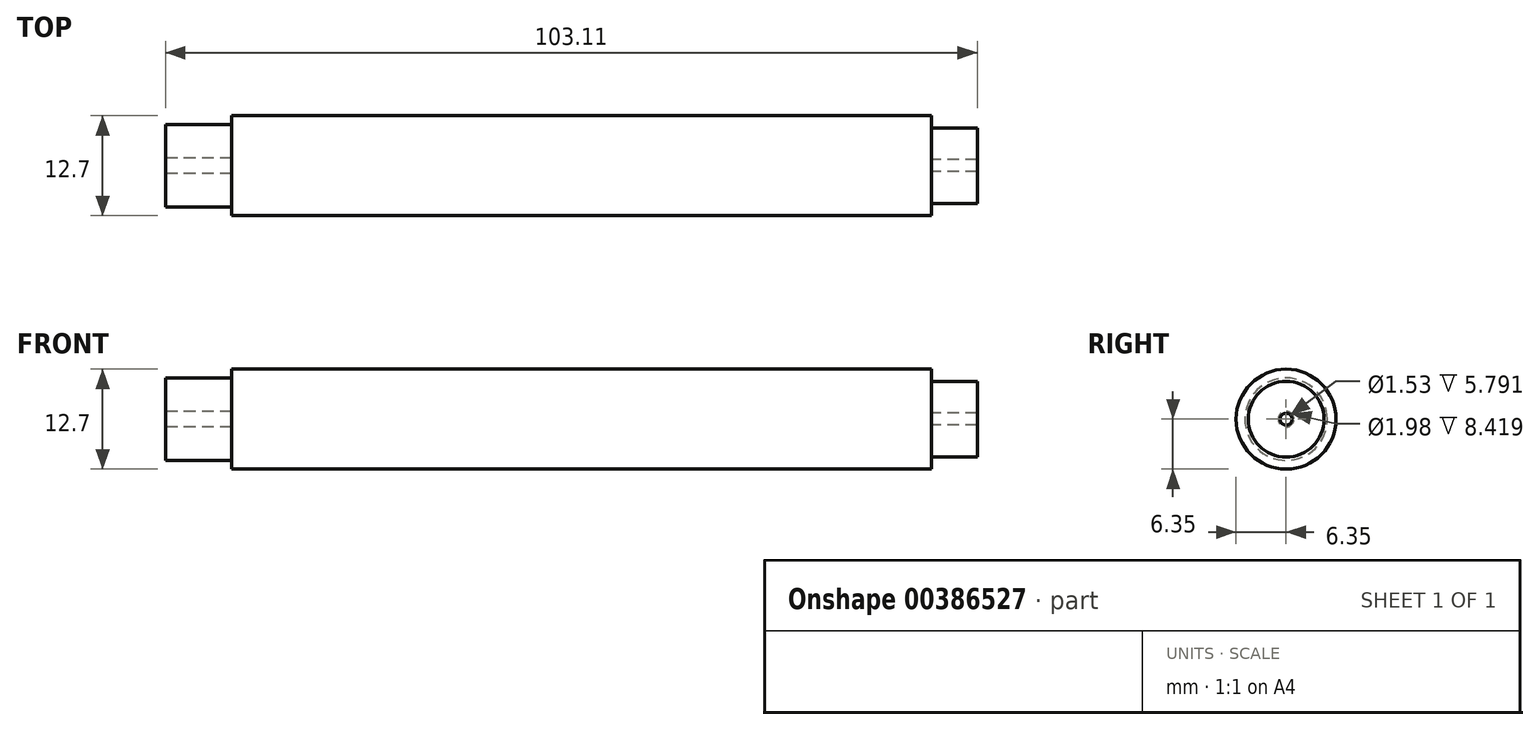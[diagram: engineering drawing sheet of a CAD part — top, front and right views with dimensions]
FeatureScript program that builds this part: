
annotation { "Feature Type Name" : "Feature", "Feature Type Description" : "" }
export const myFeature = defineFeature(function(context is Context, id is Id, definition is map)
    precondition{}
    {
        {
            var Q0;
            Q0=qCreatedBy(makeId("Front.planeOp"),FACE);
            var sketch = newSketch(context, id + "F0", { "sketchPlane" : qUnion([Q0])});
            skLineSegment(sketch, "E0.bottom", {"start": v(0, 0) * mm, "end": v(88.9, 0) * mm});
            skLineSegment(sketch, "E0.top", {"start": v(0, 6.35) * mm, "end": v(88.9, 6.35) * mm});
            skLineSegment(sketch, "E0.left", {"start": v(0, 0) * mm, "end": v(0, 6.35) * mm});
            skLineSegment(sketch, "E0.right", {"start": v(88.9, 0) * mm, "end": v(88.9, 6.35) * mm});
            skLineSegment(sketch, "E1", {"start": v(0, 0) * mm, "end": v(88.9, 0) * mm, "construction": true});
            skLineSegment(sketch, "E2.bottom", {"start": v(0, 5.23) * mm, "end": v(-8.42, 5.23) * mm});
            skLineSegment(sketch, "E2.top", {"start": v(0, 1) * mm, "end": v(-8.42, 1) * mm});
            skLineSegment(sketch, "E2.left", {"start": v(0, 5.23) * mm, "end": v(0, 1) * mm});
            skLineSegment(sketch, "E2.right", {"start": v(-8.42, 5.23) * mm, "end": v(-8.42, 1) * mm});
            skLineSegment(sketch, "E3.bottom", {"start": v(88.9, 4.8) * mm, "end": v(94.7, 4.8) * mm});
            skLineSegment(sketch, "E3.top", {"start": v(88.9, 0.76) * mm, "end": v(94.7, 0.76) * mm});
            skLineSegment(sketch, "E3.left", {"start": v(88.9, 4.8) * mm, "end": v(88.9, 0.76) * mm});
            skLineSegment(sketch, "E3.right", {"start": v(94.7, 4.8) * mm, "end": v(94.7, 0.76) * mm});
            skLineSegment(sketch, "E4", {"start": v(-8.42, 1) * mm, "end": v(0, 1) * mm, "construction": true});
            skLineSegment(sketch, "E5", {"start": v(88.9, 0.76) * mm, "end": v(94.7, 0.76) * mm, "construction": true});
            skSolve(sketch);
        }
        {
            var Q0;
            Q0=makeQuery(id+"F0.imprint","IMPRINT",FACE,{"disambiguationData":[TD([[makeQuery(id+"F0.imprint","IMPRINT",EDGE,{"derivedFrom":sQuery(id+"F0.wireOp",EDGE,"E0.bottom")}),1.0]])]});
            var Q1;
            Q1=makeQuery(id+"F0.imprint","IMPRINT",FACE,{"disambiguationData":[TD([[makeQuery(id+"F0.imprint","IMPRINT",EDGE,{"derivedFrom":sQuery(id+"F0.wireOp",EDGE,"E2.bottom")}),1.0]])]});
            var Q2;
            Q2=makeQuery(id+"F0.imprint","IMPRINT",FACE,{"disambiguationData":[TD([[makeQuery(id+"F0.imprint","IMPRINT",EDGE,{"derivedFrom":sQuery(id+"F0.wireOp",EDGE,"E3.bottom")}),-1.0]])]});
            var Q3;
            Q3=sQuery(id+"F0.wireOp",EDGE,"E0.bottom");
            revolve(context, id + "F1", {"entities" : qUnion([Q0, Q1, Q2]), "axis" : qUnion([Q3]), "revolveType" : RevolveType.FULL});
        }
    });
